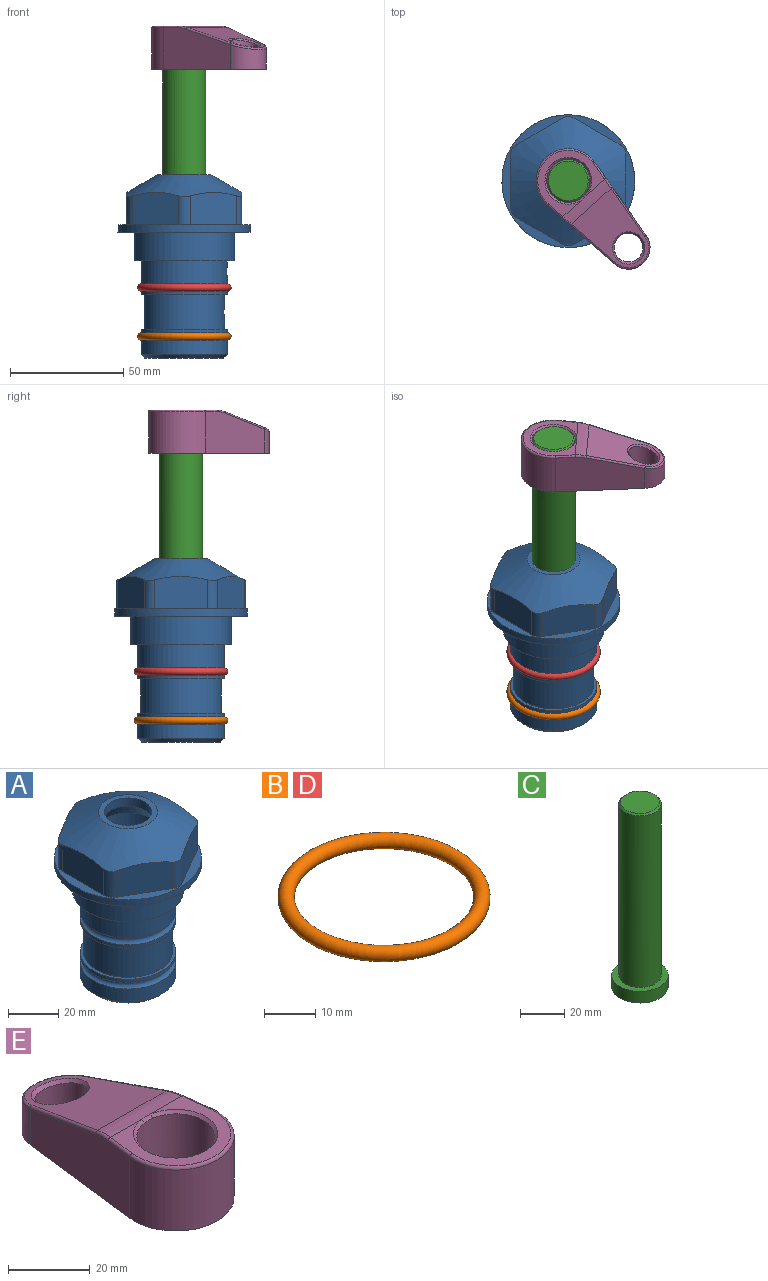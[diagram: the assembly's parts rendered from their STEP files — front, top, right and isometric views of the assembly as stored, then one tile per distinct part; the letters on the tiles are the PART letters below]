
ASSEMBLY  parts=5 mates=4
PART A: 36 faces, bbox 58.7x58.7x81 mm
  f0: cylinder r=17.78mm len=35.56mm, axis (0,0,1), area 1670.8mm2, adj f23,f24,f31
  f1: cylinder r=19.05mm len=38.1mm, axis (0,0,1), area 1191.9mm2, adj f26,f27,f30
  f2: plane 58.66x58.66mm, normal (0,0,-1), area 1150.6mm2, adj f3,f28
  f3: cylinder r=29.33mm len=58.66mm, axis (0,0,-1), area 585.1mm2, adj f2,f4
  f4: plane 58.66x58.66mm, normal (0,0,1), area 475.9mm2, adj f3,f5,f6,f7,f8,f9,f10,f11
  f5: plane 20.32x14.34mm, normal (-0.5,0.87,0), area 324.4mm2, adj f4,f15,f16,f17
  f6: plane 20.32x14.34mm, normal (0.5,0.87,0), area 324.4mm2, adj f4,f14,f15,f17
  f7: plane 23.48x14.34mm, normal (1,0,0), area 324.4mm2, adj f4,f13,f14,f17
  f8: plane 20.32x14.34mm, normal (0.5,-0.87,0), area 324.4mm2, adj f4,f12,f13,f17
  f9: plane 20.32x14.34mm, normal (-0.5,-0.87,0), area 324.4mm2, adj f4,f11,f12,f17
  f10: plane 23.48x14.34mm, normal (-1,0,0), area 324.4mm2, adj f4,f11,f16,f17
  f11: cylinder r=5.08mm len=12.85mm, axis (0,0,-1), area 67.2mm2, adj f4,f9,f10,f17
  f12: cylinder r=5.08mm len=12.85mm, axis (0,0,-1), area 67.2mm2, adj f4,f8,f9,f17
  f13: cylinder r=5.08mm len=12.85mm, axis (0,0,-1), area 67.2mm2, adj f4,f7,f8,f17
  f14: cylinder r=5.08mm len=12.85mm, axis (0,0,-1), area 67.2mm2, adj f4,f6,f7,f17
  f15: cylinder r=5.08mm len=12.85mm, axis (0,0,-1), area 67.2mm2, adj f4,f5,f6,f17
  f16: cylinder r=5.08mm len=12.85mm, axis (0,0,-1), area 67.2mm2, adj f4,f5,f10,f17
  f17: cone r=11.73mm half-angle=60deg, axis (0,0,-1), area 2071.8mm2, adj f5,f6,f7,f8,f9,f10,f11,f12
  f18: plane 23.46x23.46mm, normal (0,0,1), area 147.4mm2, adj f17,f35
  f19: plane 34.93x34.93mm, normal (0,0,-1), area 958mm2, adj f29
  f20: cylinder r=19.05mm len=38.1mm, axis (0,0,1), area 760.1mm2, adj f21,f29
  f21: torus R=19.05mm, axis (0,0,1), area 565.3mm2, adj f20,f22
  f22: cylinder r=19.05mm len=38.1mm, axis (0,0,1), area 190mm2, adj f21,f23
  f23: plane 38.1x38.1mm, normal (0,0,1), area 146.9mm2, adj f0,f22
  f24: plane 38.1x38.1mm, normal (0,0,-1), area 146.9mm2, adj f0,f25
  f25: cylinder r=19.05mm len=38.1mm, axis (0,0,1), area 190mm2, adj f24,f26
  f26: torus R=19.05mm, axis (0,0,1), area 565.3mm2, adj f1,f25
  f27: plane 44.45x44.45mm, normal (0,0,-1), area 411.7mm2, adj f1,f28
  f28: cylinder r=22.23mm len=44.45mm, axis (0,0,1), area 1773.5mm2, adj f2,f27
  f29: cone r=19.05mm half-angle=45deg, axis (0,0,1), area 257.5mm2, adj f19,f20
  f30: cylinder r=3.17mm len=6.75mm, axis (-1,0,0), area 128mm2, adj f1,f33
  f31: cylinder r=3.17mm len=6.35mm, axis (-1,0,0), area 102.5mm2, adj f0,f33
  f32: plane 25.4x25.4mm, normal (0,0,1), area 506.7mm2, adj f33
  f33: cylinder r=12.7mm len=66.42mm, axis (0,0,-1), area 5236.2mm2, adj f30,f31,f32,f34
  f34: cone r=9.53mm half-angle=30deg, axis (0,0,-1), area 443.4mm2, adj f33,f35
  f35: cylinder r=9.53mm len=19.05mm, axis (0,0,-1), area 240.9mm2, adj f18,f34
PART B: 1 faces, bbox 44.7x44.7x3.2 mm
  f0: torus R=19.05mm, axis (0,0,1), area 1193.9mm2
PART C: 6 faces, bbox 25.4x25.4x101.6 mm
  f0: plane 17.46x17.46mm, normal (0,0,1), area 239.5mm2, adj f5
  f1: plane 25.4x25.4mm, normal (0,0,-1), area 506.7mm2, adj f2
  f2: cylinder r=12.7mm len=25.4mm, axis (0,0,1), area 506.7mm2, adj f1,f3
  f3: plane 25.4x25.4mm, normal (0,0,1), area 221.7mm2, adj f2,f4
  f4: cylinder r=9.53mm len=94.46mm, axis (0,0,1), area 5653mm2, adj f3,f5
  f5: cone r=8.73mm half-angle=45deg, axis (0,0,-1), area 64.4mm2, adj f0,f4
PART D: same geometry as B
PART E: 31 faces, bbox 31.7x65.5x19.8 mm
  f0: plane 39.12x18.26mm, normal (0.99,0.12,0), area 612.2mm2, adj f1,f4,f7,f11,f13,f15
  f1: cylinder r=9.53mm len=18.91mm, axis (0,0,-1), area 296.1mm2, adj f0,f2,f7,f17
  f2: plane 39.12x18.26mm, normal (-0.99,0.12,0), area 612.2mm2, adj f1,f4,f7,f12,f14,f16
  f3: cylinder r=6.35mm len=12.7mm, axis (0,0,-1), area 362.4mm2, adj f7,f18
  f4: cylinder r=14.29mm len=28.58mm, axis (0,0,-1), area 882.2mm2, adj f0,f2,f7,f10
  f5: cylinder r=9.53mm len=19.05mm, axis (0,0,-1), area 1092.6mm2, adj f7,f19,f20
  f6: plane 26.99x23.69mm, normal (0,0,1), area 216.2mm2, adj f9,f10,f11,f12,f19
  f7: plane 63.5x28.58mm, normal (0,0,-1), area 661.8mm2, adj f0,f1,f2,f3,f4,f5,f22,f23
  f8: plane 33.52x23.6mm, normal (0,0.26,0.97), area 486mm2, adj f9,f15,f16,f17,f18
  f9: cylinder r=19.05mm len=24.72mm, axis (1,0,0), area 120.4mm2, adj f6,f8,f13,f14,f20
  f10: torus R=13.49mm, axis (0,0,1), area 59mm2, adj f4,f6,f11,f12
  f11: cylinder r=0.79mm len=8.67mm, axis (0.12,-0.99,0), area 10.8mm2, adj f0,f6,f10,f13
  f12: cylinder r=0.79mm len=8.67mm, axis (0.12,0.99,0), area 10.8mm2, adj f2,f6,f10,f14
  f13: bspline ~4.95x1.42mm, area 6.1mm2, adj f0,f9,f11,f15
  f14: bspline ~4.95x1.42mm, area 6.1mm2, adj f2,f9,f12,f16
  f15: cylinder r=0.79mm len=25.95mm, axis (0.12,-0.96,0.26), area 32.9mm2, adj f0,f8,f13,f17
  f16: cylinder r=0.79mm len=25.95mm, axis (0.12,0.96,-0.26), area 32.9mm2, adj f2,f8,f14,f17
  f17: bspline ~18.91x8.38mm, area 30mm2, adj f1,f8,f15,f16
  f18: bspline ~14.29x14.29mm, area 48.3mm2, adj f3,f8
  f19: cone r=9.53mm half-angle=45deg, axis (0,0,1), area 66.5mm2, adj f5,f6,f20
  f20: bspline ~3.22x0.96mm, area 3.5mm2, adj f5,f9,f19
  f21: plane 2.75x2.72mm, normal (0,0,-1), area 2.9mm2, adj f23,f25,f28
  f22: plane 23.05x15.88mm, normal (-0.99,-0.12,0), area 323.6mm2, adj f7,f25,f26,f27,f28,f29
  f23: plane 23.05x15.88mm, normal (0.99,-0.12,0), area 323.6mm2, adj f7,f21,f25,f27,f28,f30
  f24: cylinder r=9.53mm len=10.69mm, axis (0,0,-1), area 114.7mm2, adj f7,f27,f29,f30
  f25: cylinder r=12.7mm len=20.59mm, axis (0,0,-1), area 381.1mm2, adj f7,f21,f22,f23,f26,f28
  f26: plane 2.75x2.72mm, normal (0,0,-1), area 2.9mm2, adj f22,f25,f28
  f27: plane 19.72x18.37mm, normal (0,-0.26,-0.97), area 291.8mm2, adj f22,f23,f24,f28,f29,f30
  f28: cylinder r=15.88mm len=19.92mm, axis (1,0,0), area 54.8mm2, adj f21,f22,f23,f25,f26,f27
  f29: cylinder r=1.59mm len=11mm, axis (0,0,-1), area 34.7mm2, adj f7,f22,f24,f27
  f30: cylinder r=1.59mm len=11mm, axis (0,0,-1), area 34.7mm2, adj f7,f23,f24,f27
PLACE A at identity fixed
PLACE B t=(0,0,-21.59)mm
PLACE C rot(axis=(0,0,-1),138deg) t=(0,0,27.55)mm
PLACE D at identity
PLACE E rot(axis=(0,0,-1),138deg) t=(0,0,27.55)mm
MATE fastened C.f2 <-> E.f4  axis (0,0,1) through (0,0,91.05)mm
MATE cylindrical C.f2 <-> A.f0  axis (0,0,-1) through (0,0,-10.55)mm
MATE fastened D.f0 <-> A.f0  axis (0,0,1) through (0,0,-24.51)mm
MATE fastened B.f0 <-> A.f0  axis (0,0,1) through (0,0,-46.1)mm
